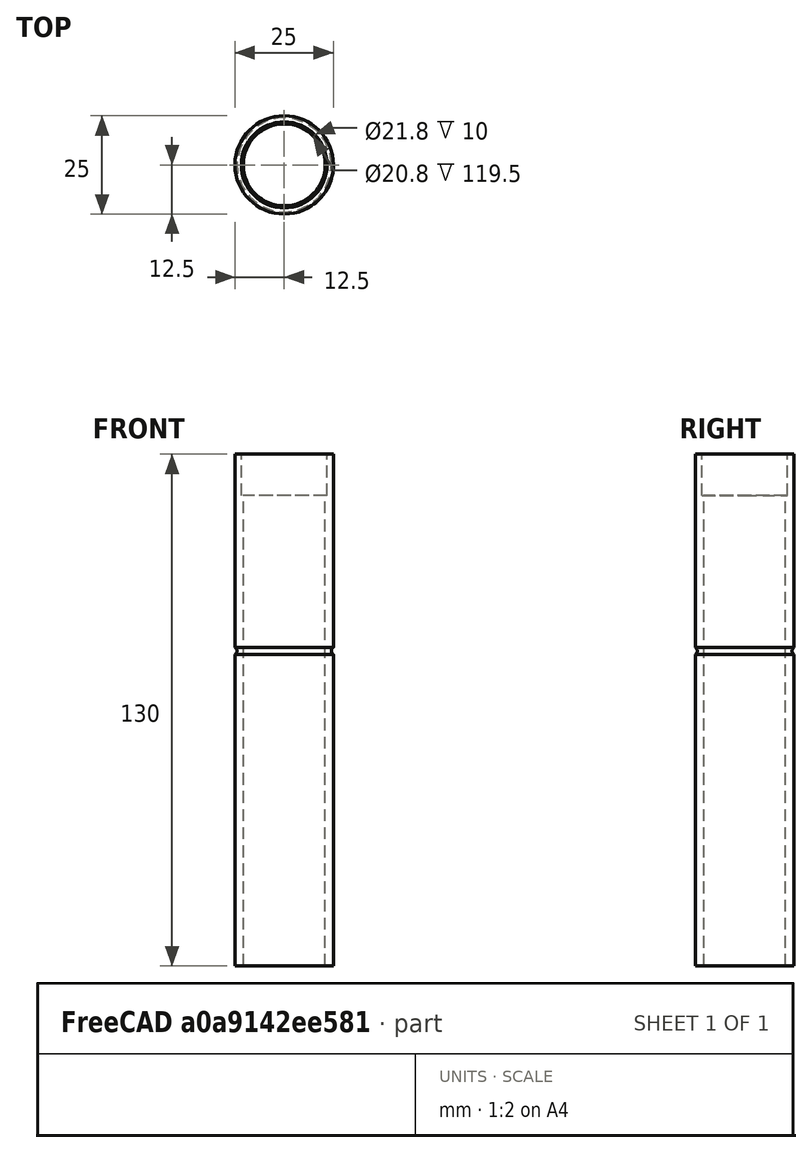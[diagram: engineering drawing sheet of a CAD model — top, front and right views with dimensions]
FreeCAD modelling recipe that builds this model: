
FCSTD DOCUMENT
Label: Part1
License: CC-BY 3.0
LicenseURL: http://creativecommons.org/licenses/by/3.0/
objects: Part::Cylinder×3, Part::Cut×3, Part::Torus×1, PartDesign::Fillet×1
note: 8 computed .brp shape members not serialized (recipe doc carries the construction recipe); baked Part::Feature solids carry a one-line shape summary decoded from their .brp

FEATURE [Part::Cylinder] Cylinder
  Angle = 360
  Height = 130
  Radius = 12.5
FEATURE [Part::Cylinder] Cylinder001
  Angle = 360
  Height = 130
  Radius = 10.4
FEATURE [Part::Cylinder] Cylinder002
  Angle = 360
  Height = 10.5
  Placement = pos=(0,0,119.5) rot=(0,0,1;0rad)
  Radius = 10.9
FEATURE [Part::Cut] Cut
  Base = -> Cylinder
  Tool = -> Cylinder001
FEATURE [Part::Cut] Cut001
  Base = -> Cut
  Tool = -> Cylinder002
FEATURE [Part::Torus] Torus001002001
  Angle1 = -180
  Angle2 = 180
  Angle3 = 360
  Placement = pos=(0,0,80) rot=(0,0,1;0rad)
  Radius1 = 13
  Radius2 = 1
FEATURE [Part::Cut] Cut002
  Base = -> Cut001
  Tool = -> Torus001002001
FEATURE [PartDesign::Fillet] Fillet
  Base = -> Cut002 [Edge6]
  Radius = 0.5
